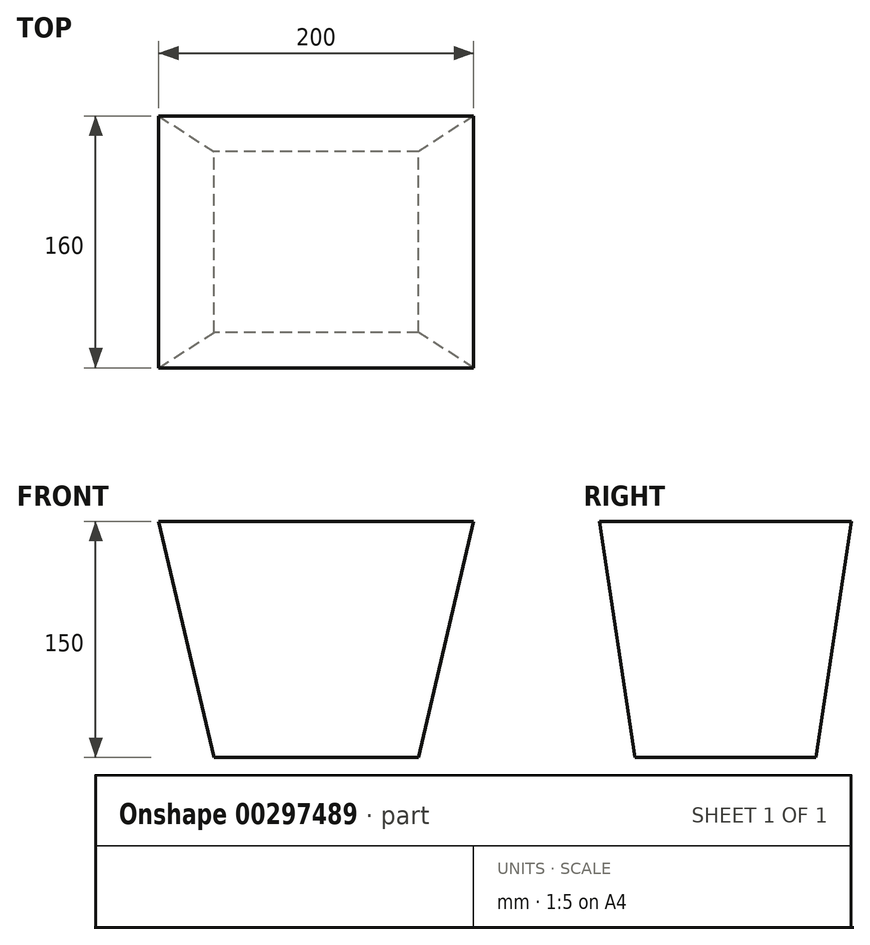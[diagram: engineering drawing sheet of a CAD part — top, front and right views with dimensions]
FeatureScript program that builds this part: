
annotation { "Feature Type Name" : "Feature", "Feature Type Description" : "" }
export const myFeature = defineFeature(function(context is Context, id is Id, definition is map)
    precondition{}
    {
        {
            var Q0;
            Q0=qCreatedBy(makeId("Top.planeOp"),FACE);
            var sketch = newSketch(context, id + "F0", { "sketchPlane" : qUnion([Q0])});
            skPoint(sketch, "E0.middle", {"position": v(0, 0) * mm});
            skLineSegment(sketch, "E1.bottom", {"start": v(65, -57.5) * mm, "end": v(-65, -57.5) * mm});
            skLineSegment(sketch, "E1.top", {"start": v(65, 57.5) * mm, "end": v(-65, 57.5) * mm});
            skLineSegment(sketch, "E1.left", {"start": v(65, -57.5) * mm, "end": v(65, 57.5) * mm});
            skLineSegment(sketch, "E1.right", {"start": v(-65, -57.5) * mm, "end": v(-65, 57.5) * mm});
            skSolve(sketch);
        }
        {
            var Q0;
            Q0=qCreatedBy(makeId("Top.planeOp"),FACE);
            cPlane(context, id + "F1", {"entities" : qUnion([Q0]), "cplaneType" : CPlaneType.OFFSET, "offset" : 150 * mm, "width" : 150 * mm, "height" : 150 * mm});
        }
        {
            var Q0;
            Q0=qCreatedBy(id+"F1.planeOp",FACE);
            var sketch = newSketch(context, id + "F2", { "sketchPlane" : qUnion([Q0])});
            skLineSegment(sketch, "E2.bottom", {"start": v(100, -80) * mm, "end": v(-100, -80) * mm});
            skLineSegment(sketch, "E2.top", {"start": v(100, 80) * mm, "end": v(-100, 80) * mm});
            skLineSegment(sketch, "E2.left", {"start": v(100, -80) * mm, "end": v(100, 80) * mm});
            skLineSegment(sketch, "E2.right", {"start": v(-100, -80) * mm, "end": v(-100, 80) * mm});
            skPoint(sketch, "E2.middle", {"position": v(0, 0) * mm});
            skSolve(sketch);
        }
        {
            var Q0;
            Q0=makeQuery(id+"F2.imprint","IMPRINT",FACE,{"disambiguationData":[TD([[makeQuery(id+"F2.imprint","IMPRINT",EDGE,{"derivedFrom":sQuery(id+"F2.wireOp",EDGE,"E2.bottom")}),-1.0]])]});
            var Q1;
            Q1=makeQuery(id+"F0.imprint","IMPRINT",FACE,{"disambiguationData":[TD([[makeQuery(id+"F0.imprint","IMPRINT",EDGE,{"derivedFrom":sQuery(id+"F0.wireOp",EDGE,"E1.bottom")}),-1.0]])]});
            loft(context, id + "F3", {"sheetProfilesArray" : [{ "sheetProfileEntities" : qUnion([Q0]) }, { "sheetProfileEntities" : qUnion([Q1]) }]});
        }
    });
